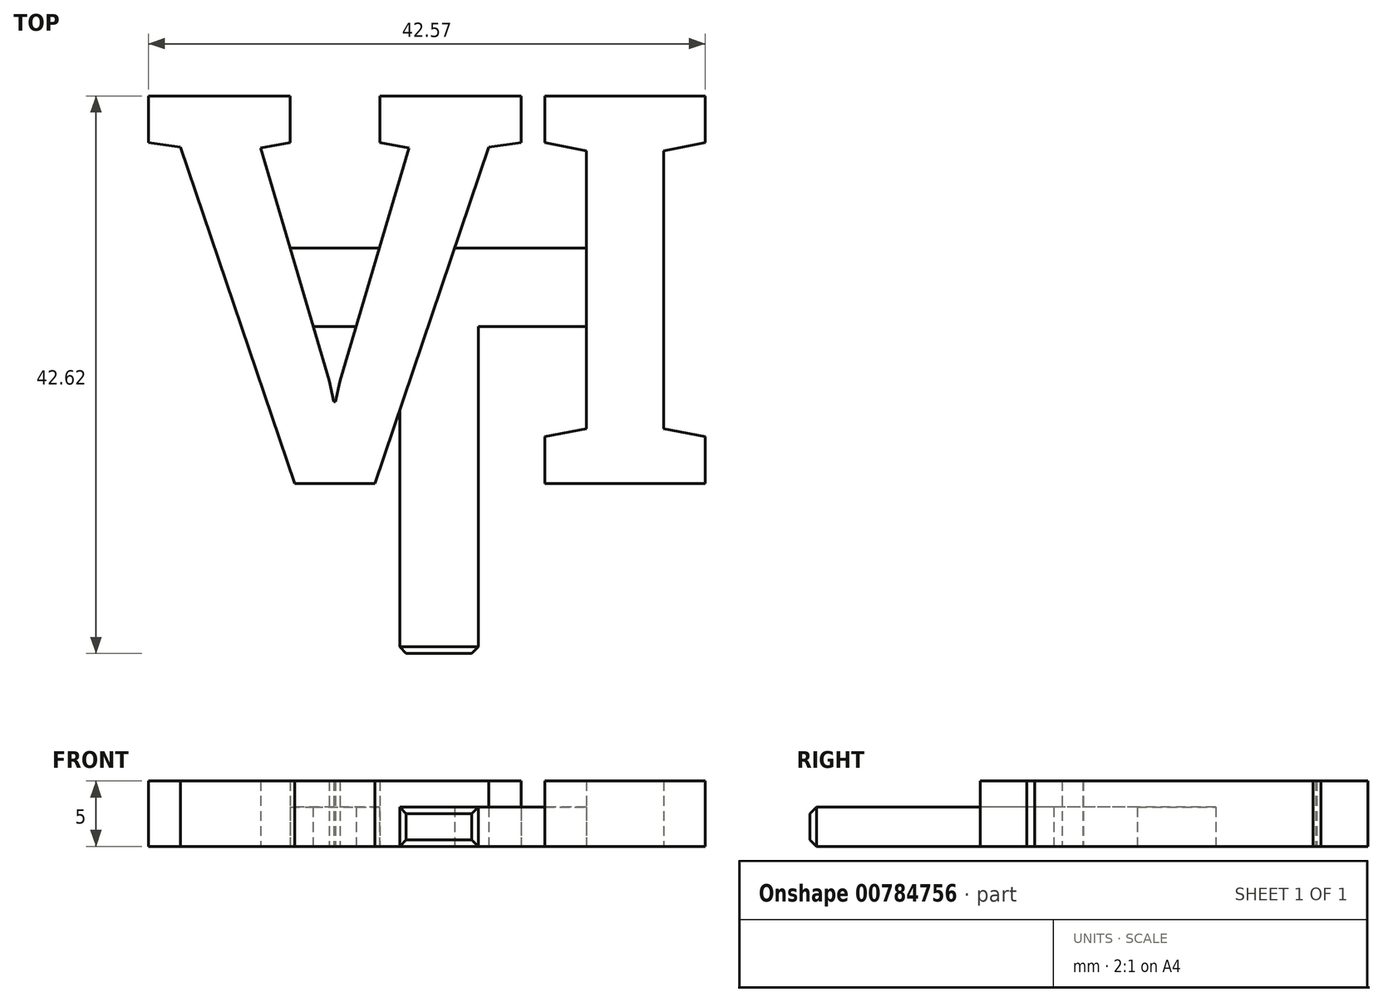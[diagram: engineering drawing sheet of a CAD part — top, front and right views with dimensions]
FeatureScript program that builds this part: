
annotation { "Feature Type Name" : "Feature", "Feature Type Description" : "" }
export const myFeature = defineFeature(function(context is Context, id is Id, definition is map)
    precondition{}
    {
        {
            var Q0;
            Q0=qCreatedBy(makeId("Top.planeOp"),FACE);
            var sketch = newSketch(context, id + "F0", { "sketchPlane" : qUnion([Q0])});
            skLineSegment(sketch, "E0.bottom", {"start": v(-15.46, 15) * mm, "end": v(4, 15) * mm, "construction": true});
            skText(sketch, "E1", { "text": "VI", "fontName": "RobotoSlab-Bold.ttf"});
            skLineSegment(sketch, "E2.bottom", {"start": v(-3, -3) * mm, "end": v(3, -3) * mm});
            skLineSegment(sketch, "E2.top", {"start": v(-3, -28) * mm, "end": v(3, -28) * mm});
            skLineSegment(sketch, "E2.left", {"start": v(-3, -3) * mm, "end": v(-3, -28) * mm});
            skLineSegment(sketch, "E2.right", {"start": v(3, -3) * mm, "end": v(3, -28) * mm});
            skLineSegment(sketch, "E3", {"start": v(-17.27, -3) * mm, "end": v(19.13, -3) * mm});
            skLineSegment(sketch, "E4", {"start": v(19.13, 3) * mm, "end": v(-17.27, 3) * mm});
            const initialGuessF0  = {"E1": [-0.0229, -0.015, 1, 0, 0.03]};
            skSetInitialGuess(sketch, initialGuessF0);
            skSolve(sketch);
        }
        {
            var Q0;
            {var subQ2=sQuery(id+"F0.wireOp",EDGE,"E1.sketch_text.stroke-0");Q0=makeQuery(id+"F0.imprint","IMPRINT",FACE,{"disambiguationData":[TD([[makeQuery(id+"F0.imprint","IMPRINT",EDGE,{"derivedFrom":subQ2}),-1.0]])]});}
            var Q1;
            {var subQ0=sQuery(id+"F0.wireOp",EDGE,"E4");var subQ1=sQuery(id+"F0.wireOp",EDGE,"E1.sketch_text.stroke-1");var subQ2=makeQuery(id+"F0.imprint","INTERSECT",VERTEX,{"derivedFrom":[subQ1,subQ0]});Q1=makeQuery(id+"F0.imprint","IMPRINT",FACE,{"disambiguationData":[TD([[makeQuery(id+"F0.imprint","IMPRINT",EDGE,{"disambiguationData":[TD([[subQ2,-1.0]])],"derivedFrom":subQ1}),-1.0]])]});}
            var Q2;
            {var subQ13=sQuery(id+"F0.wireOp",EDGE,"E1.sketch_text.stroke-2");Q2=makeQuery(id+"F0.imprint","IMPRINT",FACE,{"disambiguationData":[TD([[makeQuery(id+"F0.imprint","IMPRINT",EDGE,{"derivedFrom":subQ13}),-1.0]])]});}
            var Q3;
            {var subQ0=sQuery(id+"F0.wireOp",EDGE,"E2.bottom");var subQ1=sQuery(id+"F0.wireOp",EDGE,"E1.sketch_text.stroke-11");var subQ2=makeQuery(id+"F0.imprint","INTERSECT",VERTEX,{"derivedFrom":[subQ1,subQ0]});Q3=makeQuery(id+"F0.imprint","IMPRINT",FACE,{"disambiguationData":[TD([[makeQuery(id+"F0.imprint","IMPRINT",EDGE,{"disambiguationData":[TD([[subQ2,-1.0]])],"derivedFrom":subQ1}),-1.0]])]});}
            var Q4;
            {var subQ5=sQuery(id+"F0.wireOp",EDGE,"E1.sketch_text.stroke-5");var subQ7=sQuery(id+"F0.wireOp",EDGE,"E4");var subQ8=makeQuery(id+"F0.imprint","INTERSECT",VERTEX,{"derivedFrom":[subQ5,subQ7]});Q4=makeQuery(id+"F0.imprint","IMPRINT",FACE,{"disambiguationData":[TD([[makeQuery(id+"F0.imprint","IMPRINT",EDGE,{"disambiguationData":[TD([[subQ8,1.0]])],"derivedFrom":subQ5}),-1.0]])]});}
            var Q5;
            {var subQ0=sQuery(id+"F0.wireOp",EDGE,"E1.sketch_text.stroke-6");Q5=makeQuery(id+"F0.imprint","IMPRINT",FACE,{"disambiguationData":[TD([[makeQuery(id+"F0.imprint","IMPRINT",EDGE,{"derivedFrom":subQ0}),-1.0]])]});}
            var Q6;
            Q6=makeQuery(id+"F0.imprint","IMPRINT",FACE,{"disambiguationData":[TD([[makeQuery(id+"F0.imprint","IMPRINT",EDGE,{"derivedFrom":sQuery(id+"F0.wireOp",EDGE,"E1.sketch_text.stroke-18")}),-1.0]])]});
            var Q7;
            {var subQ0=sQuery(id+"F0.wireOp",EDGE,"E3");var subQ1=sQuery(id+"F0.wireOp",EDGE,"E1.sketch_text.stroke-22");var subQ2=makeQuery(id+"F0.imprint","INTERSECT",VERTEX,{"derivedFrom":[subQ1,subQ0]});Q7=makeQuery(id+"F0.imprint","IMPRINT",FACE,{"disambiguationData":[TD([[makeQuery(id+"F0.imprint","IMPRINT",EDGE,{"disambiguationData":[TD([[subQ2,1.0]])],"derivedFrom":subQ1}),-1.0]])]});}
            var Q8;
            {var subQ0=sQuery(id+"F0.wireOp",EDGE,"E1.sketch_text.stroke-23");Q8=makeQuery(id+"F0.imprint","IMPRINT",FACE,{"disambiguationData":[TD([[makeQuery(id+"F0.imprint","IMPRINT",EDGE,{"derivedFrom":subQ0}),-1.0]])]});}
            extrude(context, id + "F1", {"entities" : qUnion([Q0, Q1, Q2, Q3, Q4, Q5, Q6, Q7, Q8]), "depth" : 5 * mm, "offsetDistance" : 25 * mm});
        }
        {
            var Q0;
            {var subQ0=sQuery(id+"F0.wireOp",EDGE,"E4");var subQ1=sQuery(id+"F0.wireOp",EDGE,"E1.sketch_text.stroke-1");var subQ2=makeQuery(id+"F0.imprint","INTERSECT",VERTEX,{"derivedFrom":[subQ1,subQ0]});Q0=makeQuery(id+"F0.imprint","IMPRINT",FACE,{"disambiguationData":[TD([[makeQuery(id+"F0.imprint","IMPRINT",EDGE,{"disambiguationData":[TD([[subQ2,-1.0]])],"derivedFrom":subQ1}),1.0]])]});}
            var Q1;
            {var subQ1=sQuery(id+"F0.wireOp",EDGE,"E2.bottom");var subQ5=sQuery(id+"F0.wireOp",EDGE,"E1.sketch_text.stroke-11");var subQ6=makeQuery(id+"F0.imprint","INTERSECT",VERTEX,{"derivedFrom":[subQ5,subQ1]});Q1=makeQuery(id+"F0.imprint","IMPRINT",FACE,{"disambiguationData":[TD([[makeQuery(id+"F0.imprint","IMPRINT",EDGE,{"disambiguationData":[TD([[subQ6,1.0]])],"derivedFrom":subQ5}),1.0]])]});}
            var Q2;
            {var subQ0=sQuery(id+"F0.wireOp",EDGE,"E2.top");Q2=makeQuery(id+"F0.imprint","IMPRINT",FACE,{"disambiguationData":[TD([[makeQuery(id+"F0.imprint","IMPRINT",EDGE,{"derivedFrom":subQ0}),1.0]])]});}
            extrude(context, id + "F2", {"entities" : qUnion([Q0, Q1, Q2]), "operationType" : NewBodyOperationType.ADD, "depth" : 3 * mm, "offsetDistance" : 25 * mm});
        }
        {
            var Q0;
            Q0=makeQuery(id+"F2.opExtrude","SWEPT_EDGE",EDGE,{"disambiguationData":[OSD([sQuery(id+"F0.wireOp",EDGE,"E2.top"),sQuery(id+"F0.wireOp",EDGE,"E2.right")])]});
            var Q1;
            Q1=makeQuery(id+"F2.opExtrude","CAP_EDGE",EDGE,{"disambiguationData":[OSD([sQuery(id+"F0.wireOp",EDGE,"E2.top")])],"isStart":false});
            var Q2;
            Q2=makeQuery(id+"F2.opExtrude","SWEPT_EDGE",EDGE,{"disambiguationData":[OSD([sQuery(id+"F0.wireOp",EDGE,"E2.top"),sQuery(id+"F0.wireOp",EDGE,"E2.left")])]});
            var Q3;
            Q3=makeQuery(id+"F2.opExtrude","CAP_EDGE",EDGE,{"disambiguationData":[OSD([sQuery(id+"F0.wireOp",EDGE,"E2.top")])],"isStart":true});
            chamfer(context, id + "F3", {"entities" : qUnion([Q0, Q1, Q2, Q3]), "width" : 0.5 * mm, "tangentPropagation" : true});
        }
    });
